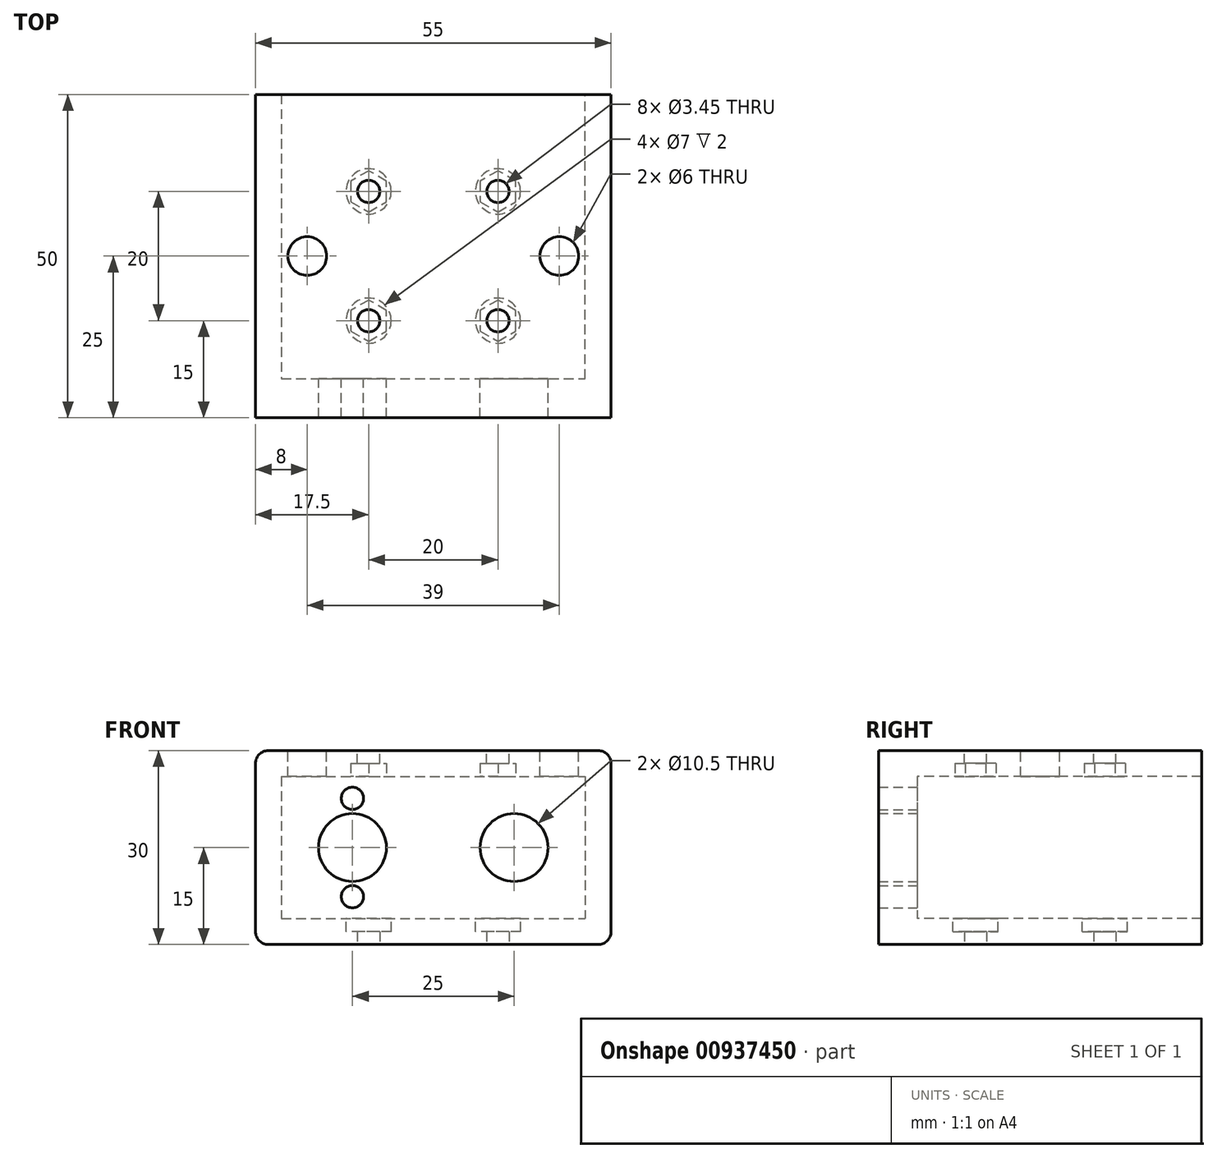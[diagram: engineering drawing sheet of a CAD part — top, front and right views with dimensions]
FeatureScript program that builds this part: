
annotation { "Feature Type Name" : "Feature", "Feature Type Description" : "" }
export const myFeature = defineFeature(function(context is Context, id is Id, definition is map)
    precondition{}
    {
        {
            var Q0;
            Q0=qCreatedBy(makeId("Top.planeOp"),FACE);
            var sketch = newSketch(context, id + "F0", { "sketchPlane" : qUnion([Q0])});
            skLineSegment(sketch, "E0.bottom", {"start": v(0, 0) * mm, "end": v(55, 0) * mm});
            skLineSegment(sketch, "E0.top", {"start": v(0, 50) * mm, "end": v(55, 50) * mm});
            skLineSegment(sketch, "E0.left", {"start": v(0, 0) * mm, "end": v(0, 50) * mm});
            skLineSegment(sketch, "E0.right", {"start": v(55, 0) * mm, "end": v(55, 50) * mm});
            skLineSegment(sketch, "E1.bottom", {"start": v(17.5, 15) * mm, "end": v(37.5, 15) * mm, "construction": true});
            skLineSegment(sketch, "E1.top", {"start": v(17.5, 35) * mm, "end": v(37.5, 35) * mm, "construction": true});
            skLineSegment(sketch, "E1.left", {"start": v(17.5, 15) * mm, "end": v(17.5, 35) * mm, "construction": true});
            skLineSegment(sketch, "E1.right", {"start": v(37.5, 15) * mm, "end": v(37.5, 35) * mm, "construction": true});
            skCircle(sketch, "E2", {"center": v(17.5, 35) * mm, "radius": 1.73 * mm});
            skCircle(sketch, "E3", {"center": v(37.5, 35) * mm, "radius": 1.73 * mm});
            skCircle(sketch, "E4", {"center": v(37.5, 15) * mm, "radius": 1.73 * mm});
            skCircle(sketch, "E5", {"center": v(17.5, 15) * mm, "radius": 1.73 * mm});
            skCircle(sketch, "E6", {"center": v(17.5, 35) * mm, "radius": 3.5 * mm});
            skCircle(sketch, "E7", {"center": v(37.5, 35) * mm, "radius": 3.5 * mm});
            skCircle(sketch, "E8", {"center": v(37.5, 15) * mm, "radius": 3.5 * mm});
            skCircle(sketch, "E9", {"center": v(17.5, 15) * mm, "radius": 3.5 * mm});
            skLineSegment(sketch, "E10", {"start": v(27.5, 0) * mm, "end": v(27.5, 15) * mm, "construction": true});
            skLineSegment(sketch, "E11", {"start": v(0, 25) * mm, "end": v(17.5, 25) * mm, "construction": true});
            skSolve(sketch);
        }
        {
            var Q0;
            Q0=qSketchRegion(id+"F0",true);
            var Q1;
            Q1=makeQuery(id+"F0.imprint","IMPRINT",FACE,{"disambiguationData":[TD([[makeQuery(id+"F0.imprint","IMPRINT",EDGE,{"derivedFrom":sQuery(id+"F0.wireOp",EDGE,"E2")}),-1.0]])]});
            var Q2;
            Q2=makeQuery(id+"F0.imprint","IMPRINT",FACE,{"disambiguationData":[TD([[makeQuery(id+"F0.imprint","IMPRINT",EDGE,{"derivedFrom":sQuery(id+"F0.wireOp",EDGE,"E3")}),-1.0]])]});
            var Q3;
            Q3=makeQuery(id+"F0.imprint","IMPRINT",FACE,{"disambiguationData":[TD([[makeQuery(id+"F0.imprint","IMPRINT",EDGE,{"derivedFrom":sQuery(id+"F0.wireOp",EDGE,"E4")}),-1.0]])]});
            var Q4;
            Q4=makeQuery(id+"F0.imprint","IMPRINT",FACE,{"disambiguationData":[TD([[makeQuery(id+"F0.imprint","IMPRINT",EDGE,{"derivedFrom":sQuery(id+"F0.wireOp",EDGE,"E5")}),-1.0]])]});
            extrude(context, id + "F1", {"entities" : qUnion([Q0, Q1, Q2, Q3, Q4]), "depth" : 4 * mm, "offsetDistance" : 25 * mm});
        }
        {
            var Q0;
            Q0=makeQuery(id+"F1.opExtrude","CAP_FACE",FACE,{"disambiguationData":[OSD([sQuery(id+"F0.wireOp",EDGE,"E0.bottom"),sQuery(id+"F0.wireOp",EDGE,"E0.top"),sQuery(id+"F0.wireOp",EDGE,"E0.left"),sQuery(id+"F0.wireOp",EDGE,"E0.right"),sQuery(id+"F0.wireOp",EDGE,"E2"),sQuery(id+"F0.wireOp",EDGE,"E3"),sQuery(id+"F0.wireOp",EDGE,"E4"),sQuery(id+"F0.wireOp",EDGE,"E5")])],"isStart":false});
            var sketch = newSketch(context, id + "F2", { "sketchPlane" : qUnion([Q0])});
            skCircle(sketch, "E12", {"center": v(17.5, 35) * mm, "radius": 3.5 * mm});
            skCircle(sketch, "E13", {"center": v(37.5, 35) * mm, "radius": 3.5 * mm});
            skCircle(sketch, "E14", {"center": v(37.5, 15) * mm, "radius": 3.5 * mm});
            skCircle(sketch, "E15", {"center": v(17.5, 15) * mm, "radius": 3.5 * mm});
            skSolve(sketch);
        }
        {
            var Q0;
            Q0=qSketchRegion(id+"F2",true);
            extrude(context, id + "F3", {"entities" : qUnion([Q0]), "operationType" : NewBodyOperationType.REMOVE, "oppositeDirection" : true, "depth" : 2 * mm, "offsetDistance" : 25 * mm});
        }
        {
            var Q0;
            Q0=makeQuery(id+"F1.opExtrude","CAP_FACE",FACE,{"disambiguationData":[OSD([sQuery(id+"F0.wireOp",EDGE,"E0.bottom"),sQuery(id+"F0.wireOp",EDGE,"E0.top"),sQuery(id+"F0.wireOp",EDGE,"E0.left"),sQuery(id+"F0.wireOp",EDGE,"E0.right"),sQuery(id+"F0.wireOp",EDGE,"E2"),sQuery(id+"F0.wireOp",EDGE,"E3"),sQuery(id+"F0.wireOp",EDGE,"E4"),sQuery(id+"F0.wireOp",EDGE,"E5")])],"isStart":false});
            var sketch = newSketch(context, id + "F4", { "sketchPlane" : qUnion([Q0])});
            skLineSegment(sketch, "E16", {"start": v(0, 50) * mm, "end": v(4, 50) * mm});
            skLineSegment(sketch, "E17", {"start": v(4, 50) * mm, "end": v(4, 6) * mm});
            skLineSegment(sketch, "E18", {"start": v(4, 6) * mm, "end": v(51, 6) * mm});
            skLineSegment(sketch, "E19", {"start": v(51, 6) * mm, "end": v(51, 50) * mm});
            skLineSegment(sketch, "E20", {"start": v(51, 50) * mm, "end": v(55, 50) * mm});
            skLineSegment(sketch, "E21", {"start": v(55, 50) * mm, "end": v(55, 0) * mm});
            skLineSegment(sketch, "E22", {"start": v(55, 0) * mm, "end": v(0, 0) * mm});
            skLineSegment(sketch, "E23", {"start": v(0, 0) * mm, "end": v(0, 50) * mm});
            skSolve(sketch);
        }
        {
            var Q0;
            Q0=qSketchRegion(id+"F4",true);
            extrude(context, id + "F5", {"entities" : qUnion([Q0]), "operationType" : NewBodyOperationType.ADD, "depth" : 22 * mm, "offsetDistance" : 25 * mm});
        }
        {
            var Q0;
            Q0=makeQuery(id+"F5.opExtrude","SWEPT_FACE",FACE,{"disambiguationData":[OSD([sQuery(id+"F4.wireOp",EDGE,"E18")])]});
            var sketch = newSketch(context, id + "F6", { "sketchPlane" : qUnion([Q0])});
            skCircle(sketch, "E24", {"center": v(-40, 15) * mm, "radius": 5.25 * mm});
            skCircle(sketch, "E25", {"center": v(-15, 22.6) * mm, "radius": 1.73 * mm});
            skCircle(sketch, "E26", {"center": v(-15, 7.4) * mm, "radius": 1.73 * mm});
            skCircle(sketch, "E27", {"center": v(-15, 15) * mm, "radius": 5.25 * mm});
            skLineSegment(sketch, "E28", {"start": v(-40, 15) * mm, "end": v(-15, 15) * mm, "construction": true});
            skLineSegment(sketch, "E29", {"start": v(-27.5, 15) * mm, "end": v(-27.5, 4) * mm, "construction": true});
            skLineSegment(sketch, "E30.0", {"start": v(-4, 4) * mm, "end": v(-51, 4) * mm});
            skSolve(sketch);
        }
        {
            var Q0;
            Q0=qSketchRegion(id+"F6",true);
            extrude(context, id + "F7", {"entities" : qUnion([Q0]), "operationType" : NewBodyOperationType.REMOVE, "endBound" : BoundingType.UP_TO_NEXT, "oppositeDirection" : true, "depth" : 25 * mm, "offsetDistance" : 25 * mm});
        }
        {
            var Q0;
            Q0=makeQuery(id+"F5.opExtrude","CAP_FACE",FACE,{"disambiguationData":[OSD([sQuery(id+"F4.wireOp",EDGE,"E16"),sQuery(id+"F4.wireOp",EDGE,"E17"),sQuery(id+"F4.wireOp",EDGE,"E18"),sQuery(id+"F4.wireOp",EDGE,"E19"),sQuery(id+"F4.wireOp",EDGE,"E20"),sQuery(id+"F4.wireOp",EDGE,"E21"),sQuery(id+"F4.wireOp",EDGE,"E22"),sQuery(id+"F4.wireOp",EDGE,"E23")])],"isStart":false});
            var sketch = newSketch(context, id + "F8", { "sketchPlane" : qUnion([Q0])});
            skLineSegment(sketch, "E31.bottom", {"start": v(0, 0) * mm, "end": v(55, 0) * mm});
            skLineSegment(sketch, "E31.top", {"start": v(0, 50) * mm, "end": v(55, 50) * mm});
            skLineSegment(sketch, "E31.left", {"start": v(0, 0) * mm, "end": v(0, 50) * mm});
            skLineSegment(sketch, "E31.right", {"start": v(55, 0) * mm, "end": v(55, 50) * mm});
            skSolve(sketch);
        }
        {
            var Q0;
            Q0=qSketchRegion(id+"F8",true);
            extrude(context, id + "F9", {"entities" : qUnion([Q0]), "operationType" : NewBodyOperationType.ADD, "depth" : 4 * mm, "offsetDistance" : 25 * mm});
        }
        {
            var Q0;
            Q0=makeQuery(id+"F9.opExtrude","CAP_EDGE",EDGE,{"disambiguationData":[OSD([sQuery(id+"F8.wireOp",EDGE,"E31.left")])],"isStart":false});
            var Q1;
            Q1=makeQuery(id+"F1.opExtrude","CAP_EDGE",EDGE,{"disambiguationData":[OSD([sQuery(id+"F0.wireOp",EDGE,"E0.left")])],"isStart":true});
            var Q2;
            Q2=makeQuery(id+"F1.opExtrude","CAP_EDGE",EDGE,{"disambiguationData":[OSD([sQuery(id+"F0.wireOp",EDGE,"E0.right")])],"isStart":true});
            var Q3;
            Q3=makeQuery(id+"F9.opExtrude","CAP_EDGE",EDGE,{"disambiguationData":[OSD([sQuery(id+"F8.wireOp",EDGE,"E31.right")])],"isStart":false});
            var Q4;
            Q4=makeQuery(id+"F5.opExtrude","CAP_EDGE",EDGE,{"disambiguationData":[OSD([sQuery(id+"F4.wireOp",EDGE,"E19")])],"isStart":false});
            var Q5;
            Q5=makeQuery(id+"F5.opExtrude","CAP_EDGE",EDGE,{"disambiguationData":[OSD([sQuery(id+"F4.wireOp",EDGE,"E17")])],"isStart":false});
            var Q6;
            Q6=makeQuery(id+"F5.opExtrude","CAP_EDGE",EDGE,{"disambiguationData":[OSD([sQuery(id+"F4.wireOp",EDGE,"E17")])],"isStart":true});
            var Q7;
            Q7=makeQuery(id+"F5.opExtrude","CAP_EDGE",EDGE,{"disambiguationData":[OSD([sQuery(id+"F4.wireOp",EDGE,"E19")])],"isStart":true});
            fillet(context, id + "F10", {"entities" : qUnion([Q0, Q1, Q2, Q3, Q4, Q5, Q6, Q7]), "radius" : 2 * mm, "tangentPropagation" : true, "allowEdgeOverflow" : false});
        }
        {
            var Q0;
            Q0=makeQuery(id+"F9.opExtrude","CAP_FACE",FACE,{"disambiguationData":[OSD([sQuery(id+"F8.wireOp",EDGE,"E31.bottom"),sQuery(id+"F8.wireOp",EDGE,"E31.top"),sQuery(id+"F8.wireOp",EDGE,"E31.left"),sQuery(id+"F8.wireOp",EDGE,"E31.right")])],"isStart":false});
            var sketch = newSketch(context, id + "F11", { "sketchPlane" : qUnion([Q0])});
            skLineSegment(sketch, "E32.bottom", {"start": v(17.5, 35) * mm, "end": v(37.5, 35) * mm, "construction": true});
            skLineSegment(sketch, "E32.top", {"start": v(17.5, 15) * mm, "end": v(37.5, 15) * mm, "construction": true});
            skLineSegment(sketch, "E32.left", {"start": v(17.5, 35) * mm, "end": v(17.5, 15) * mm, "construction": true});
            skLineSegment(sketch, "E32.right", {"start": v(37.5, 35) * mm, "end": v(37.5, 15) * mm, "construction": true});
            skLineSegment(sketch, "E33", {"start": v(2, 25) * mm, "end": v(17.5, 25) * mm, "construction": true});
            skLineSegment(sketch, "E34", {"start": v(27.5, 15) * mm, "end": v(27.5, 0) * mm, "construction": true});
            skCircle(sketch, "E35", {"center": v(17.5, 35) * mm, "radius": 1.73 * mm});
            skCircle(sketch, "E36", {"center": v(37.5, 35) * mm, "radius": 1.73 * mm});
            skCircle(sketch, "E37", {"center": v(37.5, 15) * mm, "radius": 1.73 * mm});
            skCircle(sketch, "E38", {"center": v(17.5, 15) * mm, "radius": 1.73 * mm});
            skSolve(sketch);
        }
        {
            var Q0;
            Q0=qSketchRegion(id+"F11",true);
            extrude(context, id + "F12", {"entities" : qUnion([Q0]), "operationType" : NewBodyOperationType.REMOVE, "endBound" : BoundingType.UP_TO_NEXT, "oppositeDirection" : true, "depth" : 25 * mm, "offsetDistance" : 25 * mm});
        }
        {
            var Q0;
            Q0=makeQuery(id+"F9.opExtrude","CAP_FACE",FACE,{"disambiguationData":[OSD([sQuery(id+"F8.wireOp",EDGE,"E31.bottom"),sQuery(id+"F8.wireOp",EDGE,"E31.top"),sQuery(id+"F8.wireOp",EDGE,"E31.left"),sQuery(id+"F8.wireOp",EDGE,"E31.right")])],"isStart":true});
            var sketch = newSketch(context, id + "F13", { "sketchPlane" : qUnion([Q0])});
            skCircle(sketch, "E39.cCircle", {"center": v(17.5, -15) * mm, "radius": 2.76 * mm, "construction": true});
            skLineSegment(sketch, "E39.0", {"start": v(17.5, -11.81) * mm, "end": v(20.26, -13.4) * mm});
            skLineSegment(sketch, "E39.1", {"start": v(20.26, -13.4) * mm, "end": v(20.26, -16.6) * mm});
            skLineSegment(sketch, "E39.2", {"start": v(20.26, -16.6) * mm, "end": v(17.5, -18.19) * mm});
            skLineSegment(sketch, "E39.3", {"start": v(17.5, -18.19) * mm, "end": v(14.74, -16.6) * mm});
            skLineSegment(sketch, "E39.4", {"start": v(14.74, -16.6) * mm, "end": v(14.74, -13.4) * mm});
            skLineSegment(sketch, "E39.5", {"start": v(14.74, -13.4) * mm, "end": v(17.5, -11.81) * mm});
            skPoint(sketch, "E39.0.midPoint", {"position": v(18.88, -12.6) * mm});
            skCircle(sketch, "E40.cCircle", {"center": v(37.5, -15) * mm, "radius": 2.76 * mm, "construction": true});
            skLineSegment(sketch, "E40.0", {"start": v(37.5, -11.81) * mm, "end": v(40.26, -13.4) * mm});
            skLineSegment(sketch, "E40.1", {"start": v(40.26, -13.4) * mm, "end": v(40.26, -16.6) * mm});
            skLineSegment(sketch, "E40.2", {"start": v(40.26, -16.6) * mm, "end": v(37.5, -18.19) * mm});
            skLineSegment(sketch, "E40.3", {"start": v(37.5, -18.19) * mm, "end": v(34.74, -16.6) * mm});
            skLineSegment(sketch, "E40.4", {"start": v(34.74, -16.6) * mm, "end": v(34.74, -13.4) * mm});
            skLineSegment(sketch, "E40.5", {"start": v(34.74, -13.4) * mm, "end": v(37.5, -11.81) * mm});
            skPoint(sketch, "E40.0.midPoint", {"position": v(38.88, -12.6) * mm});
            skCircle(sketch, "E41.cCircle", {"center": v(37.5, -35) * mm, "radius": 2.76 * mm, "construction": true});
            skLineSegment(sketch, "E41.0", {"start": v(37.5, -31.81) * mm, "end": v(40.26, -33.4) * mm});
            skLineSegment(sketch, "E41.1", {"start": v(40.26, -33.4) * mm, "end": v(40.26, -36.6) * mm});
            skLineSegment(sketch, "E41.2", {"start": v(40.26, -36.6) * mm, "end": v(37.5, -38.19) * mm});
            skLineSegment(sketch, "E41.3", {"start": v(37.5, -38.19) * mm, "end": v(34.74, -36.6) * mm});
            skLineSegment(sketch, "E41.4", {"start": v(34.74, -36.6) * mm, "end": v(34.74, -33.4) * mm});
            skLineSegment(sketch, "E41.5", {"start": v(34.74, -33.4) * mm, "end": v(37.5, -31.81) * mm});
            skPoint(sketch, "E41.0.midPoint", {"position": v(38.88, -32.6) * mm});
            skCircle(sketch, "E42.cCircle", {"center": v(17.5, -35) * mm, "radius": 2.76 * mm, "construction": true});
            skLineSegment(sketch, "E42.0", {"start": v(17.5, -31.81) * mm, "end": v(20.26, -33.4) * mm});
            skLineSegment(sketch, "E42.1", {"start": v(20.26, -33.4) * mm, "end": v(20.26, -36.6) * mm});
            skLineSegment(sketch, "E42.2", {"start": v(20.26, -36.6) * mm, "end": v(17.5, -38.19) * mm});
            skLineSegment(sketch, "E42.3", {"start": v(17.5, -38.19) * mm, "end": v(14.74, -36.6) * mm});
            skLineSegment(sketch, "E42.4", {"start": v(14.74, -36.6) * mm, "end": v(14.74, -33.4) * mm});
            skLineSegment(sketch, "E42.5", {"start": v(14.74, -33.4) * mm, "end": v(17.5, -31.81) * mm});
            skPoint(sketch, "E42.0.midPoint", {"position": v(18.88, -32.6) * mm});
            skSolve(sketch);
        }
        {
            var Q0;
            Q0=qSketchRegion(id+"F13",true);
            extrude(context, id + "F14", {"entities" : qUnion([Q0]), "operationType" : NewBodyOperationType.REMOVE, "oppositeDirection" : true, "depth" : 2 * mm, "offsetDistance" : 25 * mm});
        }
        {
            var Q0;
            Q0=makeQuery(id+"F9.opExtrude","CAP_FACE",FACE,{"disambiguationData":[OSD([sQuery(id+"F8.wireOp",EDGE,"E31.bottom"),sQuery(id+"F8.wireOp",EDGE,"E31.top"),sQuery(id+"F8.wireOp",EDGE,"E31.left"),sQuery(id+"F8.wireOp",EDGE,"E31.right")])],"isStart":false});
            var sketch = newSketch(context, id + "F15", { "sketchPlane" : qUnion([Q0])});
            skCircle(sketch, "E43", {"center": v(8, 25) * mm, "radius": 3 * mm});
            skCircle(sketch, "E44", {"center": v(47, 25) * mm, "radius": 3 * mm});
            skLineSegment(sketch, "E45.0", {"start": v(0, 0) * mm, "end": v(0, 50) * mm});
            skLineSegment(sketch, "E46", {"start": v(0, 25) * mm, "end": v(8, 25) * mm, "construction": true});
            skLineSegment(sketch, "E47.0", {"start": v(55, 50) * mm, "end": v(55, 0) * mm});
            skLineSegment(sketch, "E48", {"start": v(55, 25) * mm, "end": v(47, 25) * mm, "construction": true});
            skSolve(sketch);
        }
        {
            var Q0;
            Q0 = qSketchRegion(id + "F15", true);
            extrude(context, id + "F16", {"entities" : qUnion([Q0]), "operationType" : NewBodyOperationType.REMOVE, "endBound" : BoundingType.UP_TO_NEXT, "oppositeDirection" : true, "depth" : 25 * mm, "offsetDistance" : 25 * mm});
        }
    });
